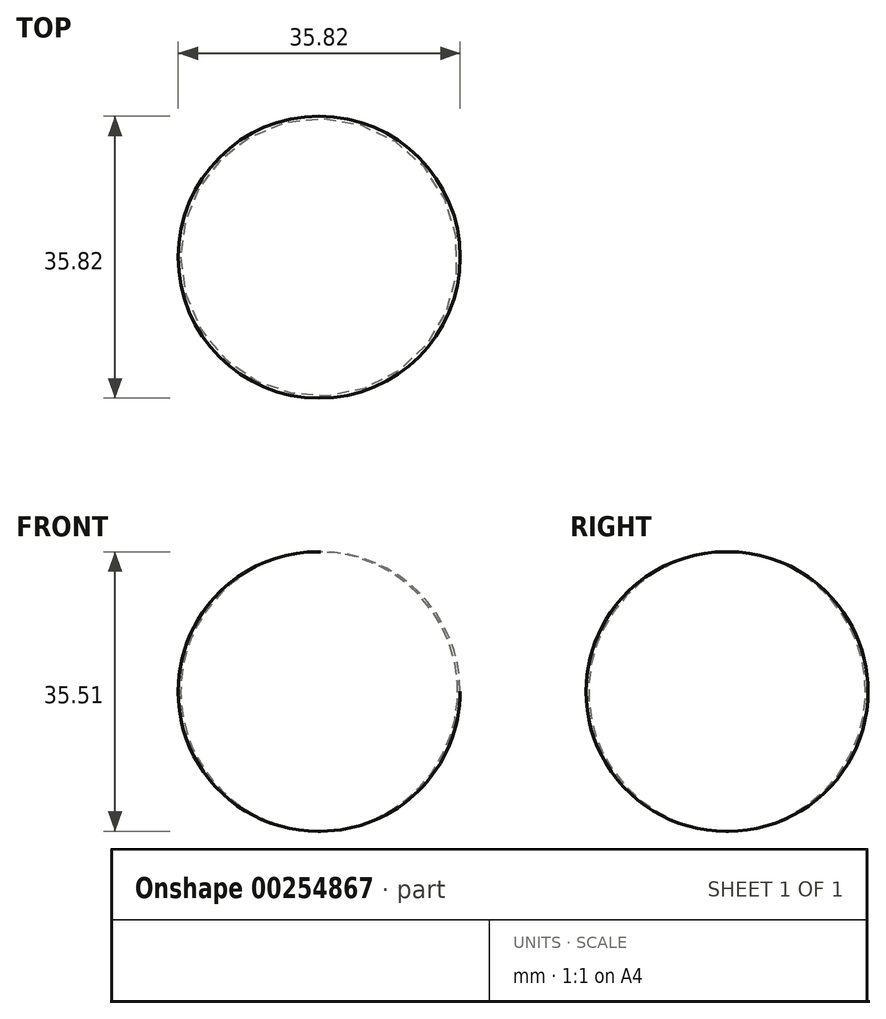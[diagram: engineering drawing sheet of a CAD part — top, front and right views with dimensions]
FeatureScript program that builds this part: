
annotation { "Feature Type Name" : "Feature", "Feature Type Description" : "" }
export const myFeature = defineFeature(function(context is Context, id is Id, definition is map)
    precondition{}
    {
        {
            var Q0;
            Q0=qCreatedBy(makeId("Front.planeOp"),FACE);
            var sketch = newSketch(context, id + "F0", { "sketchPlane" : qUnion([Q0])});
            skLineSegment(sketch, "E0", {"start": v(0, 35.5) * mm, "end": v(0, 20.63) * mm});
            skLineSegment(sketch, "E1", {"start": v(0, 20.63) * mm, "end": v(0, 0) * mm});
            skArc(sketch, "E2", {"start": v(0, 0) * mm, "mid": v(17.91, 17.75) * mm, "end": v(0, 35.5) * mm});
            skSolve(sketch);
        }
        {
            var Q0;
            Q0=makeQuery(id+"F0.imprint","IMPRINT",FACE,{"disambiguationData":[TD([[makeQuery(id+"F0.imprint","IMPRINT",EDGE,{"derivedFrom":sQuery(id+"F0.wireOp",EDGE,"E0")}),1.0]])]});
            var Q1;
            Q1=sQuery(id+"F0.wireOp",EDGE,"E1");
            revolve(context, id + "F1", {"entities" : qUnion([Q0]), "axis" : qUnion([Q1]), "revolveType" : RevolveType.FULL});
        }
    });
